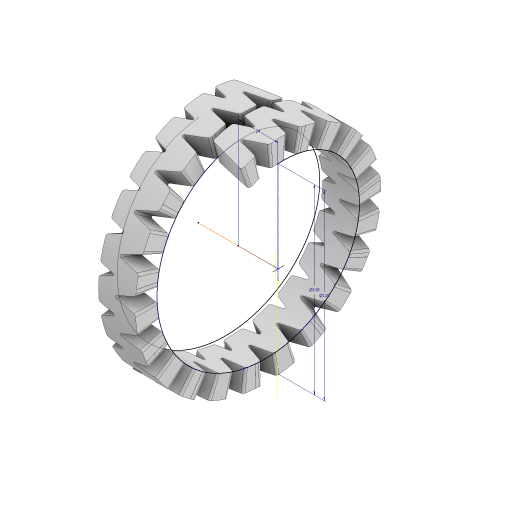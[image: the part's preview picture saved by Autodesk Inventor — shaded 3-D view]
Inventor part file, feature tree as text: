
AUTODESK INVENTOR PART (.ipt)
format: ipt  version: 2024 (Build 280153000, 153)  size: 3,709,440 bytes
history: native  units: mm
features: other x9, sketch x7, fillet x4, pattern_linear x4, extrude x3, projected_geometry x3, thicken_offset x2, move_body x2, emboss x2, direct_edit x1, boolean_combine x1
ambient origin geometry x8: Origin, YZ Plane, XZ Plane, XY Plane, X Axis, Y Axis, Z Axis, Center Point
bodies: Solid2 (feature_tree), Solid5 (feature_tree), Solid6 (feature_tree)
feature tree (38):
  other  "modulo_real.ipt"
  extrude  "Extrusion3"  Depth=10.0mm TaperAngle=0.0deg
  thicken_offset  "Thicken2"
  fillet  "Fillet2"  [1 undecoded]
  sketch  "3D Sketch1"
  other  "Work Axis1"
  move_body  "Move Body1"
  other  "Work Axis2"
  move_body  "Move Body2"
  extrude  "Extrusion1"  Depth=10.0mm TaperAngle=0.0deg
  thicken_offset  "Thicken3"
  emboss  "Emboss1"
  emboss  "Emboss2"
  extrude  "Extrusion2"  Depth=10.0mm
  direct_edit  "Direct Edit1"
  sketch  "Sketch5"  dims[d19=0.65mm d20=110.0mm d22=32.0mm]
  pattern_linear  "Rectangular Pattern1"  Count1=12 Spacing1=32.0mm
  pattern_linear  "Rectangular Pattern3"  Count1=11 Spacing1=32.0mm
  fillet  "Fillet3"  Radius=10.0mm
  pattern_linear  "Rectangular Pattern4"  Spacing1=1.5mm  [1 undecoded]
  fillet  "Fillet4"  Radius=2.15mm
  fillet  "Fillet1"  Radius=1.5mm
  pattern_linear  "Rectangular Pattern2"  Spacing1=1.5mm  [1 undecoded]
  boolean_combine  "Combine1"
  other  "contorno::modulo_real.ipt"
  other  "OperaciónIdentificador1"
  other  "Helical Curve1"
  sketch  "Sketch2"  dims[d0=10.0mm d2=24.0mm d3=10.0mm d4=110.0mm d5=0.0mm d6=-0.693513mm]
  sketch  "Sketch3"  dims[d7=10.0mm d8=25.0mm d9=0.0mm d10=0.0mm d11=13.0mm d12=0.0mm]
  sketch  "Sketch4"  dims[d13=10.0mm d14=0.0mm d15=0.693513mm d16=120.0mm d18=32.0mm]
  other  "Helical Curve2"
  sketch  "Sketch6"  dims[d23=24.0mm d24=20.0mm d25=110.0mm d26=0.0mm d29=10.0mm d30=0.0mm]
  sketch  "Sketch7"  dims[d31=1.5mm d32=1.5mm d33=2.15mm d34=1.5mm d35=1.5mm d36=10.0mm d37=0.0mm d38=-36.75mm d39=120.0mm d41=32.0mm d42=-0.675268mm d43=2.15mm d44=110.0mm d46=32.0mm d47=2.0mm]
  other  "contorno"
  projected_geometry  "Project Cut Edges2"
  projected_geometry  "Project Cut Edges3"
  projected_geometry  "Project Cut Edges4"
  other  "Size1"
note: 3 required parameter values undecoded (feature->parameter linkage not recoverable at this tier; creation-order binding heuristic only, values carry confidence <= 0.55)
